# Revit family: Shower-Showerarm-KOHLER-Alteo-K_45129
name_source: partatom
category: Plumbing Fixtures
revit_build: Autodesk Revit 2015 (Build: 20140606_1530(x64)
units: mm (PartAtom-declared; Revit-internal decimal feet)

## types (3) — shared parameters
ADA Compliant = Yes
Assembly Code = D2010700
Date Modified = 09/18/2017
Default Elevation = 72"
Description = Showerarm and flange
Flow Rate = 2 GPM
HW Connection = Yes
Height = 5 3/4"
Inlet Connection = Inlet Connection
Length = 3 23/32"
Manufacturer = Kohler
MasterFormat 1995 = 10820
MasterFormat 2004 = 10.28.13
Material = Brass Construction
Outlet Connection = Outlet Connection
Pressure = 0.00 psi
Product Documentation Link = http://www.us.kohler.com
Product Name = Alteo
Product Page URL = http://www.us.kohler.com
URL = http://www.us.kohler.com
Width = 3 23/32"

## per-type parameters (varying)
| type | CW Connection | Finish | Model | Type |
| CP-Polished Chrome | No | Metal-Kohler-CP-Polished Chrome | K-45129-CP | 1 |
| BN-Vibrant Brushed Nickel | Yes | Metal-Kohler-BN-Vibrant Brushed Nickel | K-45129-BN | 2 |
| 2BZ-Oil Rubbed Bronze | Yes | Metal-Kohler-2BZ-Oil Rubbed Bronze | K-45129-2BZ | 3 |

## geometry (parser evidence)
native form markers: Sweep x6
no freeform markers — native parametric forms only
